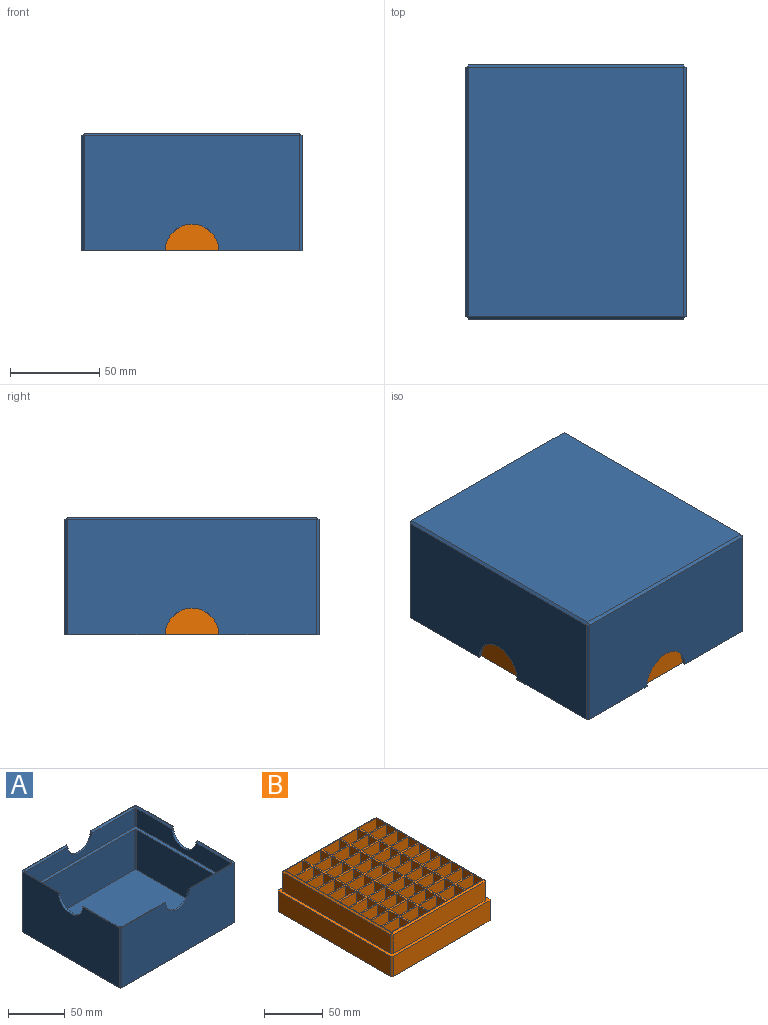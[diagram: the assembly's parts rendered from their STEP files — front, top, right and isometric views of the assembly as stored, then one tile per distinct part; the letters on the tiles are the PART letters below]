
ASSEMBLY  parts=2 mates=1
PART A: 55 faces, bbox 142.5x123.5x66 mm
  f0: plane 56.25x46.75mm, normal (0,0,1), area 54.6mm2, adj f3,f17,f25,f27,f28,f40,f52,f54
  f1: plane 56.25x46.75mm, normal (0,0,1), area 54.6mm2, adj f2,f8,f17,f31,f33,f39,f52,f53
  f2: plane 120.5x64.5mm, normal (-1,0,0), area 7418.8mm2, adj f1,f10,f39,f44,f45,f53
  f3: plane 120.5x64.5mm, normal (1,0,0), area 7418.8mm2, adj f0,f6,f40,f46,f47,f54
  f4: plane 43.33x1.5mm, normal (-0.71,0,0.71), area 91.8mm2, adj f6,f12,f30,f54
  f5: plane 43.33x1.5mm, normal (0.71,0,0.71), area 91.8mm2, adj f10,f14,f34,f53
  f6: plane 56.25x46.75mm, normal (0,0,1), area 54.6mm2, adj f3,f4,f7,f30,f32,f46,f51,f54
  f7: plane 139.5x64.5mm, normal (0,-1,0), area 8644.3mm2, adj f6,f10,f45,f46,f50,f51
  f8: plane 52.83x1.5mm, normal (0,-0.71,0.71), area 112mm2, adj f1,f15,f31,f52
  f9: plane 52.83x1.5mm, normal (0,0.71,0.71), area 112mm2, adj f10,f16,f34,f51
  f10: plane 56.25x46.75mm, normal (0,0,1), area 54.6mm2, adj f2,f5,f7,f9,f34,f45,f51,f53
  f11: plane 129.5x43mm, normal (0,1,0), area 5568.5mm2, adj f13,f19,f23,f37
  f12: plane 116.5x19.5mm, normal (-1,0,0), area 1963.2mm2, adj f4,f19,f24,f26,f27,f54
  f13: plane 132.5x113.5mm, normal (0,0,1), area 15034.2mm2, adj f11,f20,f21,f22,f23,f36,f37,f38
  f14: plane 116.5x19.5mm, normal (1,0,0), area 1963.2mm2, adj f5,f19,f29,f33,f35,f53
  f15: plane 135.5x19.5mm, normal (0,-1,0), area 2333.7mm2, adj f8,f19,f24,f28,f29,f52
  f16: plane 135.5x19.5mm, normal (0,1,0), area 2333.7mm2, adj f9,f19,f26,f32,f35,f51
  f17: plane 139.5x64.5mm, normal (0,1,0), area 8644.3mm2, adj f0,f1,f39,f40,f41,f52
  f18: plane 139.5x120.5mm, normal (0,0,-1), area 16809.8mm2, adj f41,f44,f47,f50
  f19: plane 138.5x119.5mm, normal (0,0,1), area 1512mm2, adj f11,f12,f14,f15,f16,f20,f21,f22
  f20: plane 110.5x43mm, normal (1,0,0), area 4751.5mm2, adj f13,f19,f23,f36
  f21: plane 129.5x43mm, normal (0,-1,0), area 5568.5mm2, adj f13,f19,f36,f38
  f22: plane 110.5x43mm, normal (-1,0,0), area 4751.5mm2, adj f13,f19,f37,f38
  f23: plane 43x1.5mm, normal (0.71,0.71,0), area 91.2mm2, adj f11,f13,f19,f20
  f24: plane 19.5x1.5mm, normal (-0.71,-0.71,0), area 41.4mm2, adj f12,f15,f19,f25
  f25: plane 3x3mm, normal (-0.58,-0.58,0.58), area 5.8mm2, adj f0,f24,f27,f28
  f26: plane 19.5x1.5mm, normal (-0.71,0.71,0), area 41.4mm2, adj f12,f16,f19,f30
  f27: plane 43.33x1.5mm, normal (-0.71,0,0.71), area 91.8mm2, adj f0,f12,f25,f54
  f28: plane 52.83x1.5mm, normal (0,-0.71,0.71), area 112mm2, adj f0,f15,f25,f52
  f29: plane 19.5x1.5mm, normal (0.71,-0.71,0), area 41.4mm2, adj f14,f15,f19,f31
  f30: plane 3x3mm, normal (-0.58,0.58,0.58), area 5.8mm2, adj f4,f6,f26,f32
  f31: plane 3x3mm, normal (0.58,-0.58,0.58), area 5.8mm2, adj f1,f8,f29,f33
  f32: plane 52.83x1.5mm, normal (0,0.71,0.71), area 112mm2, adj f6,f16,f30,f51
  f33: plane 43.33x1.5mm, normal (0.71,0,0.71), area 91.8mm2, adj f1,f14,f31,f53
  f34: plane 3x3mm, normal (0.58,0.58,0.58), area 5.8mm2, adj f5,f9,f10,f35
  f35: plane 19.5x1.5mm, normal (0.71,0.71,0), area 41.4mm2, adj f14,f16,f19,f34
  f36: plane 43x1.5mm, normal (0.71,-0.71,0), area 91.2mm2, adj f13,f19,f20,f21
  f37: plane 43x1.5mm, normal (-0.71,0.71,0), area 91.2mm2, adj f11,f13,f19,f22
  f38: plane 43x1.5mm, normal (-0.71,-0.71,0), area 91.2mm2, adj f13,f19,f21,f22
  f39: plane 64.5x1.5mm, normal (-0.71,0.71,0), area 136.8mm2, adj f1,f2,f17,f42
  f40: plane 64.5x1.5mm, normal (0.71,0.71,0), area 136.8mm2, adj f0,f3,f17,f43
  f41: plane 139.5x1.5mm, normal (0,0.71,-0.71), area 295.9mm2, adj f17,f18,f42,f43
  f42: plane 1.5x1.5mm, normal (-0.58,0.58,-0.58), area 1.9mm2, adj f39,f41,f44
  f43: plane 1.5x1.5mm, normal (0.58,0.58,-0.58), area 1.9mm2, adj f40,f41,f47
  f44: plane 120.5x1.5mm, normal (-0.71,0,-0.71), area 255.6mm2, adj f2,f18,f42,f48
  f45: plane 64.5x1.5mm, normal (-0.71,-0.71,0), area 136.8mm2, adj f2,f7,f10,f48
  f46: plane 64.5x1.5mm, normal (0.71,-0.71,0), area 136.8mm2, adj f3,f6,f7,f49
  f47: plane 120.5x1.5mm, normal (0.71,0,-0.71), area 255.6mm2, adj f3,f18,f43,f49
  f48: plane 1.5x1.5mm, normal (-0.58,-0.58,-0.58), area 1.9mm2, adj f44,f45,f50
  f49: plane 1.5x1.5mm, normal (0.58,-0.58,-0.58), area 1.9mm2, adj f46,f47,f50
  f50: plane 139.5x1.5mm, normal (0,-0.71,-0.71), area 295.9mm2, adj f7,f18,f48,f49
  f51: cylinder r=15mm len=30mm, axis (0,1,0), area 92mm2, adj f6,f7,f9,f10,f16,f32
  f52: cylinder r=15mm len=30mm, axis (0,1,0), area 92mm2, adj f0,f1,f8,f15,f17,f28
  f53: cylinder r=15mm len=30mm, axis (-1,0,0), area 92mm2, adj f1,f2,f5,f10,f14,f33
  f54: cylinder r=15mm len=30mm, axis (-1,0,0), area 92mm2, adj f0,f3,f4,f6,f12,f27
PART B: 277 faces, bbox 119.5x138.5x42 mm
  f0: plane 110.5x19.5mm, normal (0,1,0), area 2154.8mm2, adj f256,f261,f262,f263
  f1: plane 110.5x19.5mm, normal (0,-1,0), area 2154.8mm2, adj f256,f266,f269,f272
  f2: plane 40x11.5mm, normal (1,0,0), area 460mm2, adj f3,f203,f204,f246
  f3: plane 40x20.7mm, normal (0,-1,0), area 828mm2, adj f2,f4,f204,f246
  f4: plane 40x11.5mm, normal (-1,0,0), area 460mm2, adj f3,f203,f204,f246
  f5: plane 40x11.5mm, normal (1,0,0), area 460mm2, adj f6,f153,f204,f243
  f6: plane 40x20.7mm, normal (0,-1,0), area 828mm2, adj f5,f7,f204,f243
  f7: plane 40x11.5mm, normal (-1,0,0), area 460mm2, adj f6,f153,f204,f243
  f8: plane 40x11.5mm, normal (1,0,0), area 460mm2, adj f9,f154,f204,f238
  f9: plane 40x20.7mm, normal (0,-1,0), area 828mm2, adj f8,f10,f204,f238
  f10: plane 40x11.5mm, normal (-1,0,0), area 460mm2, adj f9,f154,f204,f238
  f11: plane 40x11.5mm, normal (1,0,0), area 460mm2, adj f12,f155,f204,f234
  f12: plane 40x20.7mm, normal (0,-1,0), area 828mm2, adj f11,f13,f204,f234
  f13: plane 40x11.5mm, normal (-1,0,0), area 460mm2, adj f12,f155,f204,f234
  f14: plane 40x11.5mm, normal (1,0,0), area 460mm2, adj f15,f156,f204,f237
  f15: plane 40x20.7mm, normal (0,-1,0), area 828mm2, adj f14,f16,f204,f237
  f16: plane 40x11.5mm, normal (-1,0,0), area 460mm2, adj f15,f156,f204,f237
  f17: plane 40x11.5mm, normal (1,0,0), area 460mm2, adj f18,f157,f204,f249
  f18: plane 40x20.7mm, normal (0,-1,0), area 828mm2, adj f17,f19,f204,f249
  f19: plane 40x11.5mm, normal (-1,0,0), area 460mm2, adj f18,f157,f204,f249
  f20: plane 40x11.5mm, normal (1,0,0), area 460mm2, adj f21,f158,f204,f252
  f21: plane 40x20.7mm, normal (0,-1,0), area 828mm2, adj f20,f22,f204,f252
  f22: plane 40x11.5mm, normal (-1,0,0), area 460mm2, adj f21,f158,f204,f252
  f23: plane 40x11.5mm, normal (1,0,0), area 460mm2, adj f24,f159,f204,f255
  f24: plane 40x20.7mm, normal (0,-1,0), area 828mm2, adj f23,f25,f204,f255
  f25: plane 40x11.5mm, normal (-1,0,0), area 460mm2, adj f24,f159,f204,f255
  f26: plane 40x11.5mm, normal (1,0,0), area 460mm2, adj f27,f160,f204,f245
  f27: plane 40x20.7mm, normal (0,-1,0), area 828mm2, adj f26,f28,f204,f245
  f28: plane 40x11.5mm, normal (-1,0,0), area 460mm2, adj f27,f160,f204,f245
  f29: plane 40x11.5mm, normal (1,0,0), area 460mm2, adj f30,f161,f204,f242
  f30: plane 40x20.7mm, normal (0,-1,0), area 828mm2, adj f29,f31,f204,f242
  f31: plane 40x11.5mm, normal (-1,0,0), area 460mm2, adj f30,f161,f204,f242
  f32: plane 40x11.5mm, normal (1,0,0), area 460mm2, adj f33,f162,f204,f239
  f33: plane 40x20.7mm, normal (0,-1,0), area 828mm2, adj f32,f34,f204,f239
  f34: plane 40x11.5mm, normal (-1,0,0), area 460mm2, adj f33,f162,f204,f239
  f35: plane 40x11.5mm, normal (1,0,0), area 460mm2, adj f36,f163,f204,f233
  f36: plane 40x20.7mm, normal (0,-1,0), area 828mm2, adj f35,f37,f204,f233
  f37: plane 40x11.5mm, normal (-1,0,0), area 460mm2, adj f36,f163,f204,f233
  f38: plane 40x11.5mm, normal (1,0,0), area 460mm2, adj f39,f164,f204,f236
  f39: plane 40x20.7mm, normal (0,-1,0), area 828mm2, adj f38,f40,f204,f236
  f40: plane 40x11.5mm, normal (-1,0,0), area 460mm2, adj f39,f164,f204,f236
  f41: plane 40x11.5mm, normal (1,0,0), area 460mm2, adj f42,f165,f204,f248
  f42: plane 40x20.7mm, normal (0,-1,0), area 828mm2, adj f41,f43,f204,f248
  f43: plane 40x11.5mm, normal (-1,0,0), area 460mm2, adj f42,f165,f204,f248
  f44: plane 40x20.7mm, normal (0,1,0), area 828mm2, adj f45,f166,f204,f254
  f45: plane 40x11.5mm, normal (1,0,0), area 460mm2, adj f44,f46,f204,f254
  f46: plane 40x20.7mm, normal (0,-1,0), area 828mm2, adj f45,f166,f204,f254
  f47: plane 40x11.5mm, normal (1,0,0), area 460mm2, adj f48,f167,f204,f251
  f48: plane 40x20.7mm, normal (0,-1,0), area 828mm2, adj f47,f49,f204,f251
  f49: plane 40x11.5mm, normal (-1,0,0), area 460mm2, adj f48,f167,f204,f251
  f50: plane 40x20.7mm, normal (0,1,0), area 828mm2, adj f51,f168,f204,f253
  f51: plane 40x11.5mm, normal (1,0,0), area 460mm2, adj f50,f52,f204,f253
  f52: plane 40x20.7mm, normal (0,-1,0), area 828mm2, adj f51,f168,f204,f253
  f53: plane 40x20.7mm, normal (0,1,0), area 828mm2, adj f54,f169,f204,f250
  f54: plane 40x11.5mm, normal (1,0,0), area 460mm2, adj f53,f55,f204,f250
  f55: plane 40x20.7mm, normal (0,-1,0), area 828mm2, adj f54,f169,f204,f250
  f56: plane 40x20.7mm, normal (0,1,0), area 828mm2, adj f57,f170,f204,f247
  f57: plane 40x11.5mm, normal (1,0,0), area 460mm2, adj f56,f58,f204,f247
  f58: plane 40x20.7mm, normal (0,-1,0), area 828mm2, adj f57,f170,f204,f247
  f59: plane 40x20.7mm, normal (0,1,0), area 828mm2, adj f60,f171,f204,f235
  f60: plane 40x11.5mm, normal (1,0,0), area 460mm2, adj f59,f61,f204,f235
  f61: plane 40x20.7mm, normal (0,-1,0), area 828mm2, adj f60,f171,f204,f235
  f62: plane 40x20.7mm, normal (0,1,0), area 828mm2, adj f63,f172,f204,f232
  f63: plane 40x11.5mm, normal (1,0,0), area 460mm2, adj f62,f64,f204,f232
  f64: plane 40x20.7mm, normal (0,-1,0), area 828mm2, adj f63,f172,f204,f232
  f65: plane 40x11.5mm, normal (1,0,0), area 460mm2, adj f66,f173,f204,f240
  f66: plane 40x20.7mm, normal (0,-1,0), area 828mm2, adj f65,f67,f204,f240
  f67: plane 40x11.5mm, normal (-1,0,0), area 460mm2, adj f66,f173,f204,f240
  f68: plane 40x20.7mm, normal (0,1,0), area 828mm2, adj f69,f174,f204,f241
  f69: plane 40x11.5mm, normal (1,0,0), area 460mm2, adj f68,f70,f204,f241
  f70: plane 40x20.7mm, normal (0,-1,0), area 828mm2, adj f69,f174,f204,f241
  f71: plane 40x20.7mm, normal (0,1,0), area 828mm2, adj f72,f175,f204,f244
  f72: plane 40x11.5mm, normal (1,0,0), area 460mm2, adj f71,f73,f204,f244
  f73: plane 40x20.7mm, normal (0,-1,0), area 828mm2, adj f72,f175,f204,f244
  f74: plane 129.5x19.5mm, normal (-1,0,0), area 2525.2mm2, adj f256,f261,f266,f267
  f75: plane 40x20.7mm, normal (0,1,0), area 828mm2, adj f76,f177,f204,f223
  f76: plane 40x11.5mm, normal (1,0,0), area 460mm2, adj f75,f77,f204,f223
  f77: plane 40x20.7mm, normal (0,-1,0), area 828mm2, adj f76,f177,f204,f223
  f78: plane 40x11.5mm, normal (1,0,0), area 460mm2, adj f79,f178,f204,f214
  f79: plane 40x20.7mm, normal (0,-1,0), area 828mm2, adj f78,f80,f204,f214
  f80: plane 40x11.5mm, normal (-1,0,0), area 460mm2, adj f79,f178,f204,f214
  f81: plane 40x11.5mm, normal (1,0,0), area 460mm2, adj f82,f179,f204,f213
  f82: plane 40x20.7mm, normal (0,-1,0), area 828mm2, adj f81,f83,f204,f213
  f83: plane 40x11.5mm, normal (-1,0,0), area 460mm2, adj f82,f179,f204,f213
  f84: plane 40x11.5mm, normal (1,0,0), area 460mm2, adj f85,f180,f204,f212
  f85: plane 40x20.7mm, normal (0,-1,0), area 828mm2, adj f84,f86,f204,f212
  f86: plane 40x11.5mm, normal (-1,0,0), area 460mm2, adj f85,f180,f204,f212
  f87: plane 40x20.7mm, normal (0,1,0), area 828mm2, adj f88,f181,f204,f211
  f88: plane 40x11.5mm, normal (1,0,0), area 460mm2, adj f87,f89,f204,f211
  f89: plane 40x20.7mm, normal (0,-1,0), area 828mm2, adj f88,f181,f204,f211
  f90: plane 40x11.5mm, normal (1,0,0), area 460mm2, adj f91,f182,f204,f218
  f91: plane 40x20.7mm, normal (0,-1,0), area 828mm2, adj f90,f92,f204,f218
  f92: plane 40x11.5mm, normal (-1,0,0), area 460mm2, adj f91,f182,f204,f218
  f93: plane 40x20.7mm, normal (0,1,0), area 828mm2, adj f94,f183,f204,f222
  f94: plane 40x11.5mm, normal (1,0,0), area 460mm2, adj f93,f95,f204,f222
  f95: plane 40x20.7mm, normal (0,-1,0), area 828mm2, adj f94,f183,f204,f222
  f96: plane 40x20.7mm, normal (0,1,0), area 828mm2, adj f97,f184,f204,f221
  f97: plane 40x11.5mm, normal (1,0,0), area 460mm2, adj f96,f98,f204,f221
  f98: plane 40x20.7mm, normal (0,-1,0), area 828mm2, adj f97,f184,f204,f221
  f99: plane 40x20.7mm, normal (0,1,0), area 828mm2, adj f100,f185,f204,f220
  f100: plane 40x11.5mm, normal (1,0,0), area 460mm2, adj f99,f101,f204,f220
  f101: plane 40x20.7mm, normal (0,-1,0), area 828mm2, adj f100,f185,f204,f220
  f102: plane 40x20.7mm, normal (0,1,0), area 828mm2, adj f103,f186,f204,f219
  f103: plane 40x11.5mm, normal (1,0,0), area 460mm2, adj f102,f104,f204,f219
  f104: plane 40x20.7mm, normal (0,-1,0), area 828mm2, adj f103,f186,f204,f219
  f105: plane 40x11.5mm, normal (1,0,0), area 460mm2, adj f106,f187,f204,f217
  f106: plane 40x20.7mm, normal (0,-1,0), area 828mm2, adj f105,f107,f204,f217
  f107: plane 40x11.5mm, normal (-1,0,0), area 460mm2, adj f106,f187,f204,f217
  f108: plane 40x11.5mm, normal (1,0,0), area 460mm2, adj f109,f188,f204,f216
  f109: plane 40x20.7mm, normal (0,-1,0), area 828mm2, adj f108,f110,f204,f216
  f110: plane 40x11.5mm, normal (-1,0,0), area 460mm2, adj f109,f188,f204,f216
  f111: plane 40x11.5mm, normal (1,0,0), area 460mm2, adj f112,f189,f204,f206
  f112: plane 40x20.7mm, normal (0,-1,0), area 828mm2, adj f111,f113,f204,f206
  f113: plane 40x11.5mm, normal (-1,0,0), area 460mm2, adj f112,f189,f204,f206
  f114: plane 40x20.7mm, normal (0,1,0), area 828mm2, adj f115,f190,f204,f207
  f115: plane 40x11.5mm, normal (1,0,0), area 460mm2, adj f114,f116,f204,f207
  f116: plane 40x20.7mm, normal (0,-1,0), area 828mm2, adj f115,f190,f204,f207
  f117: plane 40x20.7mm, normal (0,1,0), area 828mm2, adj f118,f191,f204,f208
  f118: plane 40x11.5mm, normal (1,0,0), area 460mm2, adj f117,f119,f204,f208
  f119: plane 40x20.7mm, normal (0,-1,0), area 828mm2, adj f118,f191,f204,f208
  f120: plane 40x20.7mm, normal (0,1,0), area 828mm2, adj f121,f192,f204,f209
  f121: plane 40x11.5mm, normal (1,0,0), area 460mm2, adj f120,f122,f204,f209
  f122: plane 40x20.7mm, normal (0,-1,0), area 828mm2, adj f121,f192,f204,f209
  f123: plane 40x11.5mm, normal (-1,0,0), area 460mm2, adj f124,f193,f204,f227
  f124: plane 40x20.7mm, normal (0,1,0), area 828mm2, adj f123,f125,f204,f227
  f125: plane 40x11.5mm, normal (1,0,0), area 460mm2, adj f124,f193,f204,f227
  f126: plane 40x20.7mm, normal (0,-1,0), area 828mm2, adj f127,f194,f204,f210
  f127: plane 40x11.5mm, normal (-1,0,0), area 460mm2, adj f126,f128,f204,f210
  f128: plane 40x20.7mm, normal (0,1,0), area 828mm2, adj f127,f194,f204,f210
  f129: plane 40x20.7mm, normal (0,-1,0), area 828mm2, adj f130,f195,f204,f224
  f130: plane 40x11.5mm, normal (-1,0,0), area 460mm2, adj f129,f131,f204,f224
  f131: plane 40x20.7mm, normal (0,1,0), area 828mm2, adj f130,f195,f204,f224
  f132: plane 40x20.7mm, normal (0,-1,0), area 828mm2, adj f133,f196,f204,f225
  f133: plane 40x11.5mm, normal (-1,0,0), area 460mm2, adj f132,f134,f204,f225
  f134: plane 40x20.7mm, normal (0,1,0), area 828mm2, adj f133,f196,f204,f225
  f135: plane 40x20.7mm, normal (0,-1,0), area 828mm2, adj f136,f197,f204,f226
  f136: plane 40x11.5mm, normal (-1,0,0), area 460mm2, adj f135,f137,f204,f226
  f137: plane 40x20.7mm, normal (0,1,0), area 828mm2, adj f136,f197,f204,f226
  f138: plane 40x11.5mm, normal (-1,0,0), area 460mm2, adj f139,f198,f204,f228
  f139: plane 40x20.7mm, normal (0,1,0), area 828mm2, adj f138,f140,f204,f228
  f140: plane 40x11.5mm, normal (1,0,0), area 460mm2, adj f139,f198,f204,f228
  f141: plane 40x11.5mm, normal (-1,0,0), area 460mm2, adj f142,f199,f204,f229
  f142: plane 40x20.7mm, normal (0,1,0), area 828mm2, adj f141,f143,f204,f229
  f143: plane 40x11.5mm, normal (1,0,0), area 460mm2, adj f142,f199,f204,f229
  f144: plane 40x11.5mm, normal (-1,0,0), area 460mm2, adj f145,f200,f204,f231
  f145: plane 40x20.7mm, normal (0,1,0), area 828mm2, adj f144,f146,f204,f231
  f146: plane 40x11.5mm, normal (1,0,0), area 460mm2, adj f145,f200,f204,f231
  f147: plane 40x20.7mm, normal (0,-1,0), area 828mm2, adj f148,f201,f204,f230
  f148: plane 40x11.5mm, normal (-1,0,0), area 460mm2, adj f147,f149,f204,f230
  f149: plane 40x20.7mm, normal (0,1,0), area 828mm2, adj f148,f201,f204,f230
  f150: plane 40x11.5mm, normal (-1,0,0), area 460mm2, adj f151,f202,f204,f215
  f151: plane 40x20.7mm, normal (0,1,0), area 828mm2, adj f150,f152,f204,f215
  f152: plane 40x11.5mm, normal (1,0,0), area 460mm2, adj f151,f202,f204,f215
  f153: plane 40x20.7mm, normal (0,1,0), area 828mm2, adj f5,f7,f204,f243
  f154: plane 40x20.7mm, normal (0,1,0), area 828mm2, adj f8,f10,f204,f238
  f155: plane 40x20.7mm, normal (0,1,0), area 828mm2, adj f11,f13,f204,f234
  f156: plane 40x20.7mm, normal (0,1,0), area 828mm2, adj f14,f16,f204,f237
  f157: plane 40x20.7mm, normal (0,1,0), area 828mm2, adj f17,f19,f204,f249
  f158: plane 40x20.7mm, normal (0,1,0), area 828mm2, adj f20,f22,f204,f252
  f159: plane 40x20.7mm, normal (0,1,0), area 828mm2, adj f23,f25,f204,f255
  f160: plane 40x20.7mm, normal (0,1,0), area 828mm2, adj f26,f28,f204,f245
  f161: plane 40x20.7mm, normal (0,1,0), area 828mm2, adj f29,f31,f204,f242
  f162: plane 40x20.7mm, normal (0,1,0), area 828mm2, adj f32,f34,f204,f239
  f163: plane 40x20.7mm, normal (0,1,0), area 828mm2, adj f35,f37,f204,f233
  f164: plane 40x20.7mm, normal (0,1,0), area 828mm2, adj f38,f40,f204,f236
  f165: plane 40x20.7mm, normal (0,1,0), area 828mm2, adj f41,f43,f204,f248
  f166: plane 40x11.5mm, normal (-1,0,0), area 460mm2, adj f44,f46,f204,f254
  f167: plane 40x20.7mm, normal (0,1,0), area 828mm2, adj f47,f49,f204,f251
  f168: plane 40x11.5mm, normal (-1,0,0), area 460mm2, adj f50,f52,f204,f253
  f169: plane 40x11.5mm, normal (-1,0,0), area 460mm2, adj f53,f55,f204,f250
  f170: plane 40x11.5mm, normal (-1,0,0), area 460mm2, adj f56,f58,f204,f247
  f171: plane 40x11.5mm, normal (-1,0,0), area 460mm2, adj f59,f61,f204,f235
  f172: plane 40x11.5mm, normal (-1,0,0), area 460mm2, adj f62,f64,f204,f232
  f173: plane 40x20.7mm, normal (0,1,0), area 828mm2, adj f65,f67,f204,f240
  f174: plane 40x11.5mm, normal (-1,0,0), area 460mm2, adj f68,f70,f204,f241
  f175: plane 40x11.5mm, normal (-1,0,0), area 460mm2, adj f71,f73,f204,f244
  f176: plane 129.5x19.5mm, normal (1,0,0), area 2525.2mm2, adj f256,f263,f268,f269
  f177: plane 40x11.5mm, normal (-1,0,0), area 460mm2, adj f75,f77,f204,f223
  f178: plane 40x20.7mm, normal (0,1,0), area 828mm2, adj f78,f80,f204,f214
  f179: plane 40x20.7mm, normal (0,1,0), area 828mm2, adj f81,f83,f204,f213
  f180: plane 40x20.7mm, normal (0,1,0), area 828mm2, adj f84,f86,f204,f212
  f181: plane 40x11.5mm, normal (-1,0,0), area 460mm2, adj f87,f89,f204,f211
  f182: plane 40x20.7mm, normal (0,1,0), area 828mm2, adj f90,f92,f204,f218
  f183: plane 40x11.5mm, normal (-1,0,0), area 460mm2, adj f93,f95,f204,f222
  f184: plane 40x11.5mm, normal (-1,0,0), area 460mm2, adj f96,f98,f204,f221
  f185: plane 40x11.5mm, normal (-1,0,0), area 460mm2, adj f99,f101,f204,f220
  f186: plane 40x11.5mm, normal (-1,0,0), area 460mm2, adj f102,f104,f204,f219
  f187: plane 40x20.7mm, normal (0,1,0), area 828mm2, adj f105,f107,f204,f217
  f188: plane 40x20.7mm, normal (0,1,0), area 828mm2, adj f108,f110,f204,f216
  f189: plane 40x20.7mm, normal (0,1,0), area 828mm2, adj f111,f113,f204,f206
  f190: plane 40x11.5mm, normal (-1,0,0), area 460mm2, adj f114,f116,f204,f207
  f191: plane 40x11.5mm, normal (-1,0,0), area 460mm2, adj f117,f119,f204,f208
  f192: plane 40x11.5mm, normal (-1,0,0), area 460mm2, adj f120,f122,f204,f209
  f193: plane 40x20.7mm, normal (0,-1,0), area 828mm2, adj f123,f125,f204,f227
  f194: plane 40x11.5mm, normal (1,0,0), area 460mm2, adj f126,f128,f204,f210
  f195: plane 40x11.5mm, normal (1,0,0), area 460mm2, adj f129,f131,f204,f224
  f196: plane 40x11.5mm, normal (1,0,0), area 460mm2, adj f132,f134,f204,f225
  f197: plane 40x11.5mm, normal (1,0,0), area 460mm2, adj f135,f137,f204,f226
  f198: plane 40x20.7mm, normal (0,-1,0), area 828mm2, adj f138,f140,f204,f228
  f199: plane 40x20.7mm, normal (0,-1,0), area 828mm2, adj f141,f143,f204,f229
  f200: plane 40x20.7mm, normal (0,-1,0), area 828mm2, adj f144,f146,f204,f231
  f201: plane 40x11.5mm, normal (1,0,0), area 460mm2, adj f147,f149,f204,f230
  f202: plane 40x20.7mm, normal (0,-1,0), area 828mm2, adj f150,f152,f204,f215
  f203: plane 40x20.7mm, normal (0,1,0), area 828mm2, adj f2,f4,f204,f246
  f204: plane 129.5x110.5mm, normal (0,0,1), area 2407.3mm2, adj f2,f3,f4,f5,f6,f7,f8,f9
  f205: plane 138.5x119.5mm, normal (0,0,-1), area 16546.2mm2, adj f257,f258,f259,f260,f273,f274,f275,f276
  f206: plane 20.7x11.5mm, normal (0,0,1), area 238mm2, adj f111,f112,f113,f189
  f207: plane 20.7x11.5mm, normal (0,0,1), area 238mm2, adj f114,f115,f116,f190
  f208: plane 20.7x11.5mm, normal (0,0,1), area 238mm2, adj f117,f118,f119,f191
  f209: plane 20.7x11.5mm, normal (0,0,1), area 238.1mm2, adj f120,f121,f122,f192
  f210: plane 20.7x11.5mm, normal (0,0,1), area 238.1mm2, adj f126,f127,f128,f194
  f211: plane 20.7x11.5mm, normal (0,0,1), area 238.1mm2, adj f87,f88,f89,f181
  f212: plane 20.7x11.5mm, normal (0,0,1), area 238.1mm2, adj f84,f85,f86,f180
  f213: plane 20.7x11.5mm, normal (0,0,1), area 238.1mm2, adj f81,f82,f83,f179
  f214: plane 20.7x11.5mm, normal (0,0,1), area 238mm2, adj f78,f79,f80,f178
  f215: plane 20.7x11.5mm, normal (0,0,1), area 238mm2, adj f150,f151,f152,f202
  f216: plane 20.7x11.5mm, normal (0,0,1), area 238mm2, adj f108,f109,f110,f188
  f217: plane 20.7x11.5mm, normal (0,0,1), area 238mm2, adj f105,f106,f107,f187
  f218: plane 20.7x11.5mm, normal (0,0,1), area 238.1mm2, adj f90,f91,f92,f182
  f219: plane 20.7x11.5mm, normal (0,0,1), area 238.1mm2, adj f102,f103,f104,f186
  f220: plane 20.7x11.5mm, normal (0,0,1), area 238.1mm2, adj f99,f100,f101,f185
  f221: plane 20.7x11.5mm, normal (0,0,1), area 238.1mm2, adj f96,f97,f98,f184
  f222: plane 20.7x11.5mm, normal (0,0,1), area 238.1mm2, adj f93,f94,f95,f183
  f223: plane 20.7x11.5mm, normal (0,0,1), area 238.1mm2, adj f75,f76,f77,f177
  f224: plane 20.7x11.5mm, normal (0,0,1), area 238.1mm2, adj f129,f130,f131,f195
  f225: plane 20.7x11.5mm, normal (0,0,1), area 238.1mm2, adj f132,f133,f134,f196
  f226: plane 20.7x11.5mm, normal (0,0,1), area 238.1mm2, adj f135,f136,f137,f197
  f227: plane 20.7x11.5mm, normal (0,0,1), area 238.1mm2, adj f123,f124,f125,f193
  f228: plane 20.7x11.5mm, normal (0,0,1), area 238.1mm2, adj f138,f139,f140,f198
  f229: plane 20.7x11.5mm, normal (0,0,1), area 238.1mm2, adj f141,f142,f143,f199
  f230: plane 20.7x11.5mm, normal (0,0,1), area 238mm2, adj f147,f148,f149,f201
  f231: plane 20.7x11.5mm, normal (0,0,1), area 238mm2, adj f144,f145,f146,f200
  f232: plane 20.7x11.5mm, normal (0,0,1), area 238.1mm2, adj f62,f63,f64,f172
  f233: plane 20.7x11.5mm, normal (0,0,1), area 238mm2, adj f35,f36,f37,f163
  f234: plane 20.7x11.5mm, normal (0,0,1), area 238.1mm2, adj f11,f12,f13,f155
  f235: plane 20.7x11.5mm, normal (0,0,1), area 238.1mm2, adj f59,f60,f61,f171
  f236: plane 20.7x11.5mm, normal (0,0,1), area 238mm2, adj f38,f39,f40,f164
  f237: plane 20.7x11.5mm, normal (0,0,1), area 238.1mm2, adj f14,f15,f16,f156
  f238: plane 20.7x11.5mm, normal (0,0,1), area 238.1mm2, adj f8,f9,f10,f154
  f239: plane 20.7x11.5mm, normal (0,0,1), area 238.1mm2, adj f32,f33,f34,f162
  f240: plane 20.7x11.5mm, normal (0,0,1), area 238.1mm2, adj f65,f66,f67,f173
  f241: plane 20.7x11.5mm, normal (0,0,1), area 238.1mm2, adj f68,f69,f70,f174
  f242: plane 20.7x11.5mm, normal (0,0,1), area 238mm2, adj f29,f30,f31,f161
  f243: plane 20.7x11.5mm, normal (0,0,1), area 238mm2, adj f5,f6,f7,f153
  f244: plane 20.7x11.5mm, normal (0,0,1), area 238mm2, adj f71,f72,f73,f175
  f245: plane 20.7x11.5mm, normal (0,0,1), area 238mm2, adj f26,f27,f28,f160
  f246: plane 20.7x11.5mm, normal (0,0,1), area 238mm2, adj f2,f3,f4,f203
  f247: plane 20.7x11.5mm, normal (0,0,1), area 238.1mm2, adj f56,f57,f58,f170
  f248: plane 20.7x11.5mm, normal (0,0,1), area 238.1mm2, adj f41,f42,f43,f165
  f249: plane 20.7x11.5mm, normal (0,0,1), area 238.1mm2, adj f17,f18,f19,f157
  f250: plane 20.7x11.5mm, normal (0,0,1), area 238.1mm2, adj f53,f54,f55,f169
  f251: plane 20.7x11.5mm, normal (0,0,1), area 238mm2, adj f47,f48,f49,f167
  f252: plane 20.7x11.5mm, normal (0,0,1), area 238.1mm2, adj f20,f21,f22,f158
  f253: plane 20.7x11.5mm, normal (0,0,1), area 238mm2, adj f50,f51,f52,f168
  f254: plane 20.7x11.5mm, normal (0,0,1), area 238mm2, adj f44,f45,f46,f166
  f255: plane 20.7x11.5mm, normal (0,0,1), area 238mm2, adj f23,f24,f25,f159
  f256: plane 138.5x119.5mm, normal (0,0,1), area 1512mm2, adj f0,f1,f74,f176,f257,f258,f259,f260
  f257: plane 135.5x21mm, normal (1,0,0), area 2845.5mm2, adj f205,f256,f273,f275
  f258: plane 116.5x21mm, normal (0,-1,0), area 2446.5mm2, adj f205,f256,f275,f276
  f259: plane 135.5x21mm, normal (-1,0,0), area 2845.5mm2, adj f205,f256,f274,f276
  f260: plane 116.5x21mm, normal (0,1,0), area 2446.5mm2, adj f205,f256,f273,f274
  f261: plane 19.5x1.5mm, normal (-0.71,0.71,0), area 41.4mm2, adj f0,f74,f256,f264
  f262: plane 110.5x1.5mm, normal (0,0.71,0.71), area 234.4mm2, adj f0,f204,f264,f265
  f263: plane 19.5x1.5mm, normal (0.71,0.71,0), area 41.4mm2, adj f0,f176,f256,f265
  f264: plane 1.5x1.5mm, normal (-0.58,0.58,0.58), area 1.9mm2, adj f261,f262,f267
  f265: plane 1.5x1.5mm, normal (0.58,0.58,0.58), area 1.9mm2, adj f262,f263,f268
  f266: plane 19.5x1.5mm, normal (-0.71,-0.71,0), area 41.4mm2, adj f1,f74,f256,f270
  f267: plane 129.5x1.5mm, normal (-0.71,0,0.71), area 274.7mm2, adj f74,f204,f264,f270
  f268: plane 129.5x1.5mm, normal (0.71,0,0.71), area 274.7mm2, adj f176,f204,f265,f271
  f269: plane 19.5x1.5mm, normal (0.71,-0.71,0), area 41.4mm2, adj f1,f176,f256,f271
  f270: plane 1.5x1.5mm, normal (-0.58,-0.58,0.58), area 1.9mm2, adj f266,f267,f272
  f271: plane 1.5x1.5mm, normal (0.58,-0.58,0.58), area 1.9mm2, adj f268,f269,f272
  f272: plane 110.5x1.5mm, normal (0,-0.71,0.71), area 234.4mm2, adj f1,f204,f270,f271
  f273: plane 21x1.5mm, normal (0.71,0.71,0), area 44.5mm2, adj f205,f256,f257,f260
  f274: plane 21x1.5mm, normal (-0.71,0.71,0), area 44.5mm2, adj f205,f256,f259,f260
  f275: plane 21x1.5mm, normal (0.71,-0.71,0), area 44.5mm2, adj f205,f256,f257,f258
  f276: plane 21x1.5mm, normal (-0.71,-0.71,0), area 44.5mm2, adj f205,f256,f258,f259
PLACE A rot(axis=(0.71,-0.71,0),180deg) t=(0,0,66)mm
PLACE B at identity fixed
MATE slider A.f19 <-> B.f256  axis (0,0,-1) through (0,-66.25,21)mm
